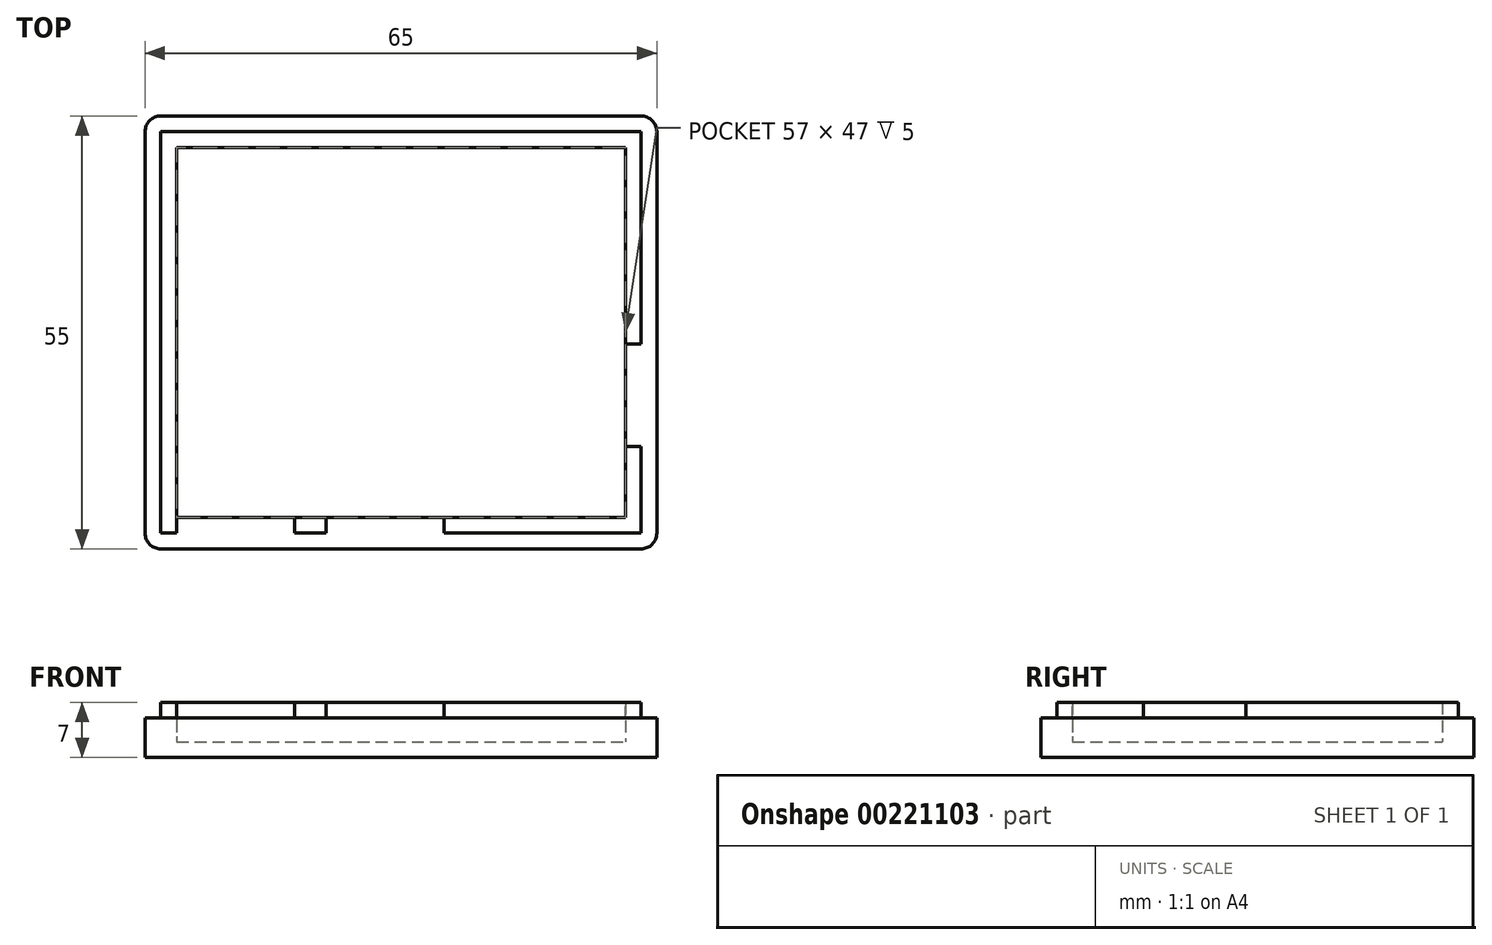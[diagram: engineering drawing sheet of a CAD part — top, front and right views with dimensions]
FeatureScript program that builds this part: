
annotation { "Feature Type Name" : "Feature", "Feature Type Description" : "" }
export const myFeature = defineFeature(function(context is Context, id is Id, definition is map)
    precondition{}
    {
        {
            var Q0;
            Q0=qCreatedBy(makeId("Top.planeOp"),FACE);
            var sketch = newSketch(context, id + "F0", { "sketchPlane" : qUnion([Q0])});
            skLineSegment(sketch, "E0.bottom", {"start": v(32.5, 27.5) * mm, "end": v(-32.5, 27.5) * mm});
            skLineSegment(sketch, "E0.top", {"start": v(32.5, -27.5) * mm, "end": v(-32.5, -27.5) * mm});
            skLineSegment(sketch, "E0.left", {"start": v(32.5, 27.5) * mm, "end": v(32.5, -27.5) * mm});
            skLineSegment(sketch, "E0.right", {"start": v(-32.5, 27.5) * mm, "end": v(-32.5, -27.5) * mm});
            skPoint(sketch, "E0.middle", {"position": v(0, 0) * mm});
            skSolve(sketch);
        }
        {
            var Q0;
            Q0=makeQuery(id+"F0.imprint","IMPRINT",FACE,{"disambiguationData":[TD([[makeQuery(id+"F0.imprint","IMPRINT",EDGE,{"derivedFrom":sQuery(id+"F0.wireOp",EDGE,"E0.bottom")}),1.0]])]});
            extrude(context, id + "F1", {"entities" : qUnion([Q0]), "endBound" : BoundingType.SYMMETRIC, "depth" : 5 * mm});
        }
        {
            var Q0;
            Q0=makeQuery(id+"F1.opExtrude","CAP_FACE",FACE,{"disambiguationData":[OSD([sQuery(id+"F0.wireOp",EDGE,"E0.bottom"),sQuery(id+"F0.wireOp",EDGE,"E0.top"),sQuery(id+"F0.wireOp",EDGE,"E0.left"),sQuery(id+"F0.wireOp",EDGE,"E0.right")])],"isStart":true});
            shell(context, id + "F2", {"entities" : qUnion([Q0]), "thickness" : 2 * mm});
        }
        {
            var Q0;
            Q0=makeQuery(id+"F1.opExtrude","SWEPT_BODY",BODY,{"disambiguationData":[OSD([sQuery(id+"F0.wireOp",EDGE,"E0.bottom"),sQuery(id+"F0.wireOp",EDGE,"E0.top"),sQuery(id+"F0.wireOp",EDGE,"E0.left"),sQuery(id+"F0.wireOp",EDGE,"E0.right")])]});
            var Q1;
            {var subQ0=sQuery(id+"F0.wireOp",EDGE,"E0.bottom");Q1=makeQuery(id+"F2.opShell","OFFSET_EDGE",EDGE,{"disambiguationData":[OSD([subQ0]),TDD([makeQuery(id+"F1.opExtrude","CAP_EDGE",EDGE,{"disambiguationData":[OSD([subQ0])],"isStart":true})])]});}
            transform(context, id + "F3", {"entities" : qUnion([Q0]), "transformType" : TransformType.ROTATION, "transformAxis" : qUnion([Q1]), "angle" : 180 * degree, "makeCopy" : false});
        }
        {
            var Q0;
            Q0=makeQuery(id+"F1.opExtrude","SWEPT_BODY",BODY,{"disambiguationData":[OSD([sQuery(id+"F0.wireOp",EDGE,"E0.bottom"),sQuery(id+"F0.wireOp",EDGE,"E0.top"),sQuery(id+"F0.wireOp",EDGE,"E0.left"),sQuery(id+"F0.wireOp",EDGE,"E0.right")])]});
            transform(context, id + "F4", {"entities" : qUnion([Q0]), "transformType" : TransformType.TRANSLATION_3D, "dx" : -0.76 * mm, "dy" : -36.83 * mm, "dz" : 3.8 * mm, "makeCopy" : false});
        }
        {
            var Q0;
            Q0=makeQuery(id+"F1.opExtrude","SWEPT_BODY",BODY,{"disambiguationData":[OSD([sQuery(id+"F0.wireOp",EDGE,"E0.bottom"),sQuery(id+"F0.wireOp",EDGE,"E0.top"),sQuery(id+"F0.wireOp",EDGE,"E0.left"),sQuery(id+"F0.wireOp",EDGE,"E0.right")])]});
            transform(context, id + "F5", {"entities" : qUnion([Q0]), "transformType" : TransformType.TRANSLATION_3D, "dx" : 0.89 * mm, "dy" : -3.7 * mm, "dz" : 1.14 * mm, "makeCopy" : false});
        }
        {
            var Q0;
            Q0=makeQuery(id+"F2.opShell","OFFSET_FACE",FACE,{"disambiguationData":[OSD([sQuery(id+"F0.wireOp",EDGE,"E0.bottom"),sQuery(id+"F0.wireOp",EDGE,"E0.top"),sQuery(id+"F0.wireOp",EDGE,"E0.left"),sQuery(id+"F0.wireOp",EDGE,"E0.right")])]});
            var sketch = newSketch(context, id + "F6", { "sketchPlane" : qUnion([Q0])});
            skLineSegment(sketch, "E1.0", {"start": v(28.63, 33.96) * mm, "end": v(-28.37, 33.96) * mm});
            skLineSegment(sketch, "E1.1", {"start": v(28.63, -13.04) * mm, "end": v(28.63, 33.96) * mm});
            skLineSegment(sketch, "E1.2", {"start": v(-28.37, -13.04) * mm, "end": v(28.63, -13.04) * mm});
            skLineSegment(sketch, "E1.3", {"start": v(-28.37, 33.96) * mm, "end": v(-28.37, -13.04) * mm});
            skSolve(sketch);
        }
        {
            var Q0;
            Q0=makeQuery(id+"F6.imprint","IMPRINT",FACE,{"disambiguationData":[TD([[makeQuery(id+"F6.imprint","IMPRINT",EDGE,{"derivedFrom":sQuery(id+"F6.wireOp",EDGE,"E1.0")}),-1.0]])]});
            extrude(context, id + "F7", {"entities" : qUnion([Q0]), "operationType" : NewBodyOperationType.ADD, "depth" : 5 * mm});
        }
        {
            var Q0;
            Q0=makeQuery(id+"F1.opExtrude","SWEPT_EDGE",EDGE,{"disambiguationData":[OSD([sQuery(id+"F0.wireOp",EDGE,"E0.bottom"),sQuery(id+"F0.wireOp",EDGE,"E0.right")])]});
            var Q1;
            Q1=makeQuery(id+"F1.opExtrude","SWEPT_EDGE",EDGE,{"disambiguationData":[OSD([sQuery(id+"F0.wireOp",EDGE,"E0.bottom"),sQuery(id+"F0.wireOp",EDGE,"E0.left")])]});
            var Q2;
            Q2=makeQuery(id+"F1.opExtrude","SWEPT_EDGE",EDGE,{"disambiguationData":[OSD([sQuery(id+"F0.wireOp",EDGE,"E0.top"),sQuery(id+"F0.wireOp",EDGE,"E0.left")])]});
            var Q3;
            Q3=makeQuery(id+"F1.opExtrude","SWEPT_EDGE",EDGE,{"disambiguationData":[OSD([sQuery(id+"F0.wireOp",EDGE,"E0.top"),sQuery(id+"F0.wireOp",EDGE,"E0.right")])]});
            fillet(context, id + "F8", {"entities" : qUnion([Q0, Q1, Q2, Q3]), "radius" : 2 * mm, "tangentPropagation" : true, "allowEdgeOverflow" : false});
        }
        {
            var Q0;
            Q0=makeQuery(id+"F1.opExtrude","SWEPT_FACE",FACE,{"disambiguationData":[OSD([sQuery(id+"F0.wireOp",EDGE,"E0.bottom")])]});
            var sketch = newSketch(context, id + "F9", { "sketchPlane" : qUnion([Q0])});
            skLineSegment(sketch, "E2.bottom", {"start": v(-28.37, 4.45) * mm, "end": v(-13.37, 4.45) * mm});
            skLineSegment(sketch, "E2.top", {"start": v(-28.37, 2.45) * mm, "end": v(-13.37, 2.45) * mm});
            skLineSegment(sketch, "E2.left", {"start": v(-28.37, 4.45) * mm, "end": v(-28.37, 2.45) * mm});
            skLineSegment(sketch, "E2.right", {"start": v(-13.37, 4.45) * mm, "end": v(-13.37, 2.45) * mm});
            skLineSegment(sketch, "E3.bottom", {"start": v(-9.37, 4.45) * mm, "end": v(5.63, 4.45) * mm});
            skLineSegment(sketch, "E3.top", {"start": v(-9.37, 2.45) * mm, "end": v(5.63, 2.45) * mm});
            skLineSegment(sketch, "E3.left", {"start": v(-9.37, 4.45) * mm, "end": v(-9.37, 2.45) * mm});
            skLineSegment(sketch, "E3.right", {"start": v(5.63, 4.45) * mm, "end": v(5.63, 2.45) * mm});
            skSolve(sketch);
        }
        {
            var Q0;
            Q0=makeQuery(id+"F9.imprint","IMPRINT",FACE,{"disambiguationData":[TD([[makeQuery(id+"F9.imprint","IMPRINT",EDGE,{"derivedFrom":sQuery(id+"F9.wireOp",EDGE,"E2.bottom")}),-1.0]])]});
            var Q1;
            {var subQ0=sQuery(id+"F9.wireOp",EDGE,"E3.bottom");Q1=makeQuery(id+"F9.imprint","IMPRINT",FACE,{"disambiguationData":[TD([[makeQuery(id+"F9.imprint","IMPRINT",EDGE,{"derivedFrom":subQ0}),-1.0]])]});}
            extrude(context, id + "F10", {"entities" : qUnion([Q0, Q1]), "operationType" : NewBodyOperationType.REMOVE, "oppositeDirection" : true, "depth" : 25 * mm});
        }
        {
            var Q0;
            Q0=makeQuery(id+"F1.opExtrude","SWEPT_FACE",FACE,{"disambiguationData":[OSD([sQuery(id+"F0.wireOp",EDGE,"E0.left")])]});
            var sketch = newSketch(context, id + "F11", { "sketchPlane" : qUnion([Q0])});
            skLineSegment(sketch, "E4.bottom", {"start": v(-4.04, 4.45) * mm, "end": v(8.96, 4.45) * mm});
            skLineSegment(sketch, "E4.top", {"start": v(-4.04, 2.45) * mm, "end": v(8.96, 2.45) * mm});
            skLineSegment(sketch, "E4.left", {"start": v(-4.04, 4.45) * mm, "end": v(-4.04, 2.45) * mm});
            skLineSegment(sketch, "E4.right", {"start": v(8.96, 4.45) * mm, "end": v(8.96, 2.45) * mm});
            skSolve(sketch);
        }
        {
            var Q0;
            Q0=makeQuery(id+"F11.imprint","IMPRINT",FACE,{"disambiguationData":[TD([[makeQuery(id+"F11.imprint","IMPRINT",EDGE,{"derivedFrom":sQuery(id+"F11.wireOp",EDGE,"E4.bottom")}),-1.0]])]});
            extrude(context, id + "F12", {"entities" : qUnion([Q0]), "operationType" : NewBodyOperationType.REMOVE, "oppositeDirection" : true, "depth" : 25 * mm});
        }
    });
